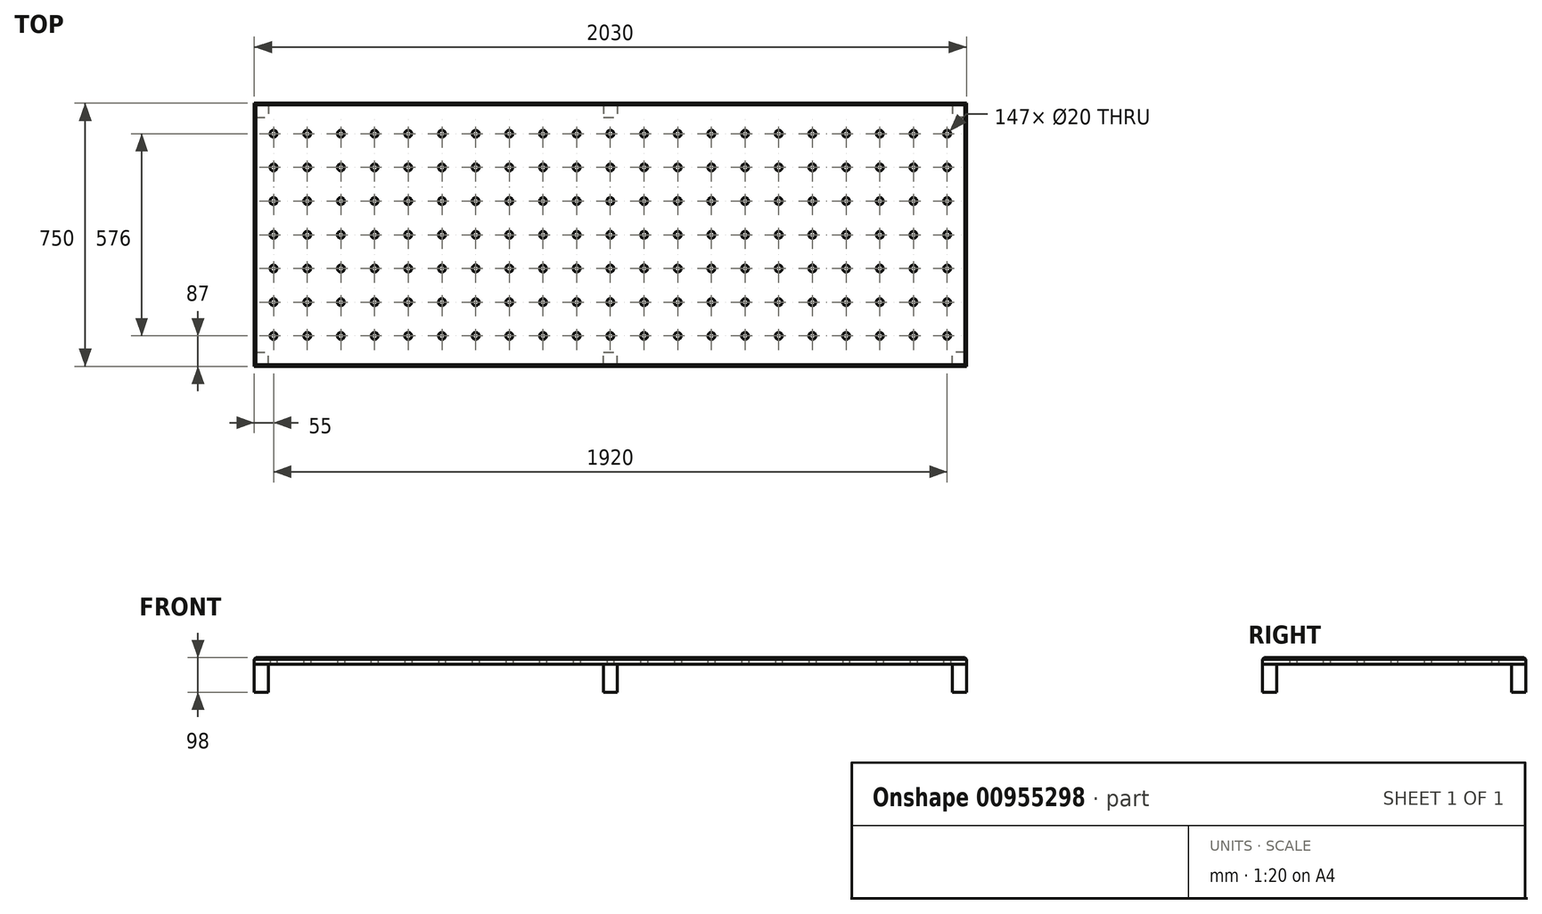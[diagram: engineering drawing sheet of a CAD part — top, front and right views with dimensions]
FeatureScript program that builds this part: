
annotation { "Feature Type Name" : "Feature", "Feature Type Description" : "" }
export const myFeature = defineFeature(function(context is Context, id is Id, definition is map)
    precondition{}
    {
        {
            var Q0;
            Q0=qCreatedBy(makeId("Top.planeOp"),FACE);
            var sketch = newSketch(context, id + "F0", { "sketchPlane" : qUnion([Q0])});
            skLineSegment(sketch, "E0.bottom", {"start": v(-1015, 375) * mm, "end": v(1015, 375) * mm});
            skLineSegment(sketch, "E0.top", {"start": v(-1015, -375) * mm, "end": v(1015, -375) * mm});
            skLineSegment(sketch, "E0.left", {"start": v(-1015, 375) * mm, "end": v(-1015, -375) * mm});
            skLineSegment(sketch, "E0.right", {"start": v(1015, 375) * mm, "end": v(1015, -375) * mm});
            skPoint(sketch, "E0.middle", {"position": v(0, 0) * mm});
            skLineSegment(sketch, "E1", {"start": v(-1321.87, 0) * mm, "end": v(1540.38, 0) * mm, "construction": true});
            skCircle(sketch, "E2", {"center": v(0, 0) * mm, "radius": 10 * mm});
            skCircle(sketch, "E3.0.1.0", {"center": v(0, 96) * mm, "radius": 10 * mm});
            skCircle(sketch, "E3.0.2.0", {"center": v(0, 192) * mm, "radius": 10 * mm});
            skCircle(sketch, "E3.0.3.0", {"center": v(0, 288) * mm, "radius": 10 * mm});
            skCircle(sketch, "E3.1.0.0", {"center": v(96, 0) * mm, "radius": 10 * mm});
            skCircle(sketch, "E3.1.1.0", {"center": v(96, 96) * mm, "radius": 10 * mm});
            skCircle(sketch, "E3.1.2.0", {"center": v(96, 192) * mm, "radius": 10 * mm});
            skCircle(sketch, "E3.1.3.0", {"center": v(96, 288) * mm, "radius": 10 * mm});
            skCircle(sketch, "E3.2.0.0", {"center": v(192, 0) * mm, "radius": 10 * mm});
            skCircle(sketch, "E3.2.1.0", {"center": v(192, 96) * mm, "radius": 10 * mm});
            skCircle(sketch, "E3.2.2.0", {"center": v(192, 192) * mm, "radius": 10 * mm});
            skCircle(sketch, "E3.2.3.0", {"center": v(192, 288) * mm, "radius": 10 * mm});
            skCircle(sketch, "E3.3.0.0", {"center": v(288, 0) * mm, "radius": 10 * mm});
            skCircle(sketch, "E3.3.1.0", {"center": v(288, 96) * mm, "radius": 10 * mm});
            skCircle(sketch, "E3.3.2.0", {"center": v(288, 192) * mm, "radius": 10 * mm});
            skCircle(sketch, "E3.3.3.0", {"center": v(288, 288) * mm, "radius": 10 * mm});
            skCircle(sketch, "E3.4.0.0", {"center": v(384, 0) * mm, "radius": 10 * mm});
            skCircle(sketch, "E3.4.1.0", {"center": v(384, 96) * mm, "radius": 10 * mm});
            skCircle(sketch, "E3.4.2.0", {"center": v(384, 192) * mm, "radius": 10 * mm});
            skCircle(sketch, "E3.4.3.0", {"center": v(384, 288) * mm, "radius": 10 * mm});
            skCircle(sketch, "E3.5.0.0", {"center": v(480, 0) * mm, "radius": 10 * mm});
            skCircle(sketch, "E3.5.1.0", {"center": v(480, 96) * mm, "radius": 10 * mm});
            skCircle(sketch, "E3.5.2.0", {"center": v(480, 192) * mm, "radius": 10 * mm});
            skCircle(sketch, "E3.5.3.0", {"center": v(480, 288) * mm, "radius": 10 * mm});
            skCircle(sketch, "E3.6.0.0", {"center": v(576, 0) * mm, "radius": 10 * mm});
            skCircle(sketch, "E3.6.1.0", {"center": v(576, 96) * mm, "radius": 10 * mm});
            skCircle(sketch, "E3.6.2.0", {"center": v(576, 192) * mm, "radius": 10 * mm});
            skCircle(sketch, "E3.6.3.0", {"center": v(576, 288) * mm, "radius": 10 * mm});
            skCircle(sketch, "E3.7.0.0", {"center": v(672, 0) * mm, "radius": 10 * mm});
            skCircle(sketch, "E3.7.1.0", {"center": v(672, 96) * mm, "radius": 10 * mm});
            skCircle(sketch, "E3.7.2.0", {"center": v(672, 192) * mm, "radius": 10 * mm});
            skCircle(sketch, "E3.7.3.0", {"center": v(672, 288) * mm, "radius": 10 * mm});
            skCircle(sketch, "E3.8.0.0", {"center": v(768, 0) * mm, "radius": 10 * mm});
            skCircle(sketch, "E3.8.1.0", {"center": v(768, 96) * mm, "radius": 10 * mm});
            skCircle(sketch, "E3.8.2.0", {"center": v(768, 192) * mm, "radius": 10 * mm});
            skCircle(sketch, "E3.8.3.0", {"center": v(768, 288) * mm, "radius": 10 * mm});
            skCircle(sketch, "E3.9.0.0", {"center": v(864, 0) * mm, "radius": 10 * mm});
            skCircle(sketch, "E3.9.1.0", {"center": v(864, 96) * mm, "radius": 10 * mm});
            skCircle(sketch, "E3.9.2.0", {"center": v(864, 192) * mm, "radius": 10 * mm});
            skCircle(sketch, "E3.9.3.0", {"center": v(864, 288) * mm, "radius": 10 * mm});
            skCircle(sketch, "E3.10.0.0", {"center": v(960, 0) * mm, "radius": 10 * mm});
            skCircle(sketch, "E3.10.1.0", {"center": v(960, 96) * mm, "radius": 10 * mm});
            skCircle(sketch, "E3.10.2.0", {"center": v(960, 192) * mm, "radius": 10 * mm});
            skCircle(sketch, "E3.10.3.0", {"center": v(960, 288) * mm, "radius": 10 * mm});
            skLineSegment(sketch, "E3.direction1", {"start": v(0, 0) * mm, "end": v(96, 0) * mm, "construction": true});
            skLineSegment(sketch, "E3.direction2", {"start": v(0, 0) * mm, "end": v(0, 96) * mm, "construction": true});
            skCircle(sketch, "E4.MirrorC", {"center": v(768, -96) * mm, "radius": 10 * mm});
            skCircle(sketch, "E5.MirrorC", {"center": v(480, -288) * mm, "radius": 10 * mm});
            skCircle(sketch, "E6.MirrorC", {"center": v(384, -192) * mm, "radius": 10 * mm});
            skCircle(sketch, "E7.MirrorC", {"center": v(96, -96) * mm, "radius": 10 * mm});
            skCircle(sketch, "E8.MirrorC", {"center": v(864, -192) * mm, "radius": 10 * mm});
            skCircle(sketch, "E9.MirrorC", {"center": v(96, -192) * mm, "radius": 10 * mm});
            skCircle(sketch, "E10.MirrorC", {"center": v(768, -192) * mm, "radius": 10 * mm});
            skCircle(sketch, "E11.MirrorC", {"center": v(192, -192) * mm, "radius": 10 * mm});
            skCircle(sketch, "E12.MirrorC", {"center": v(960, -192) * mm, "radius": 10 * mm});
            skCircle(sketch, "E13.MirrorC", {"center": v(960, -288) * mm, "radius": 10 * mm});
            skCircle(sketch, "E14.MirrorC", {"center": v(960, -96) * mm, "radius": 10 * mm});
            skCircle(sketch, "E15.MirrorC", {"center": v(192, -96) * mm, "radius": 10 * mm});
            skCircle(sketch, "E16.MirrorC", {"center": v(576, -288) * mm, "radius": 10 * mm});
            skCircle(sketch, "E17.MirrorC", {"center": v(192, -288) * mm, "radius": 10 * mm});
            skCircle(sketch, "E18.MirrorC", {"center": v(96, -288) * mm, "radius": 10 * mm});
            skCircle(sketch, "E19.MirrorC", {"center": v(672, -288) * mm, "radius": 10 * mm});
            skCircle(sketch, "E20.MirrorC", {"center": v(384, -288) * mm, "radius": 10 * mm});
            skCircle(sketch, "E21.MirrorC", {"center": v(576, -96) * mm, "radius": 10 * mm});
            skCircle(sketch, "E22.MirrorC", {"center": v(768, -288) * mm, "radius": 10 * mm});
            skCircle(sketch, "E23.MirrorC", {"center": v(480, -96) * mm, "radius": 10 * mm});
            skCircle(sketch, "E24.MirrorC", {"center": v(480, -192) * mm, "radius": 10 * mm});
            skCircle(sketch, "E25.MirrorC", {"center": v(288, -288) * mm, "radius": 10 * mm});
            skCircle(sketch, "E26.MirrorC", {"center": v(864, -288) * mm, "radius": 10 * mm});
            skCircle(sketch, "E27.MirrorC", {"center": v(384, -96) * mm, "radius": 10 * mm});
            skCircle(sketch, "E28.MirrorC", {"center": v(288, -96) * mm, "radius": 10 * mm});
            skCircle(sketch, "E29.MirrorC", {"center": v(288, -192) * mm, "radius": 10 * mm});
            skCircle(sketch, "E30.MirrorC", {"center": v(864, -96) * mm, "radius": 10 * mm});
            skCircle(sketch, "E31.MirrorC", {"center": v(576, -192) * mm, "radius": 10 * mm});
            skCircle(sketch, "E32.MirrorC", {"center": v(672, -192) * mm, "radius": 10 * mm});
            skCircle(sketch, "E33.MirrorC", {"center": v(672, -96) * mm, "radius": 10 * mm});
            skCircle(sketch, "E34.MirrorC", {"center": v(-96, 0) * mm, "radius": 10 * mm});
            skCircle(sketch, "E35.MirrorC", {"center": v(-960, 192) * mm, "radius": 10 * mm});
            skCircle(sketch, "E36.MirrorC", {"center": v(-480, 0) * mm, "radius": 10 * mm});
            skCircle(sketch, "E37.MirrorC", {"center": v(-192, 288) * mm, "radius": 10 * mm});
            skCircle(sketch, "E38.MirrorC", {"center": v(-480, 96) * mm, "radius": 10 * mm});
            skCircle(sketch, "E39.MirrorC", {"center": v(-768, 0) * mm, "radius": 10 * mm});
            skCircle(sketch, "E40.MirrorC", {"center": v(-768, -288) * mm, "radius": 10 * mm});
            skCircle(sketch, "E41.MirrorC", {"center": v(-480, 192) * mm, "radius": 10 * mm});
            skCircle(sketch, "E42.MirrorC", {"center": v(-576, 96) * mm, "radius": 10 * mm});
            skCircle(sketch, "E43.MirrorC", {"center": v(-672, 192) * mm, "radius": 10 * mm});
            skCircle(sketch, "E44.MirrorC", {"center": v(-960, -192) * mm, "radius": 10 * mm});
            skCircle(sketch, "E45.MirrorC", {"center": v(-960, 0) * mm, "radius": 10 * mm});
            skCircle(sketch, "E46.MirrorC", {"center": v(-480, -288) * mm, "radius": 10 * mm});
            skCircle(sketch, "E47.MirrorC", {"center": v(-768, -192) * mm, "radius": 10 * mm});
            skCircle(sketch, "E48.MirrorC", {"center": v(-960, 96) * mm, "radius": 10 * mm});
            skCircle(sketch, "E49.MirrorC", {"center": v(-768, 192) * mm, "radius": 10 * mm});
            skCircle(sketch, "E50.MirrorC", {"center": v(-288, 192) * mm, "radius": 10 * mm});
            skCircle(sketch, "E51.MirrorC", {"center": v(-288, -192) * mm, "radius": 10 * mm});
            skCircle(sketch, "E52.MirrorC", {"center": v(-192, -192) * mm, "radius": 10 * mm});
            skCircle(sketch, "E53.MirrorC", {"center": v(-288, 288) * mm, "radius": 10 * mm});
            skCircle(sketch, "E54.MirrorC", {"center": v(-192, 0) * mm, "radius": 10 * mm});
            skCircle(sketch, "E55.MirrorC", {"center": v(-672, 288) * mm, "radius": 10 * mm});
            skCircle(sketch, "E56.MirrorC", {"center": v(-576, 192) * mm, "radius": 10 * mm});
            skCircle(sketch, "E57.MirrorC", {"center": v(-672, -192) * mm, "radius": 10 * mm});
            skCircle(sketch, "E58.MirrorC", {"center": v(-768, -96) * mm, "radius": 10 * mm});
            skCircle(sketch, "E59.MirrorC", {"center": v(-384, -288) * mm, "radius": 10 * mm});
            skCircle(sketch, "E60.MirrorC", {"center": v(-384, -96) * mm, "radius": 10 * mm});
            skCircle(sketch, "E61.MirrorC", {"center": v(-192, -288) * mm, "radius": 10 * mm});
            skCircle(sketch, "E62.MirrorC", {"center": v(-864, 288) * mm, "radius": 10 * mm});
            skCircle(sketch, "E63.MirrorC", {"center": v(-576, -96) * mm, "radius": 10 * mm});
            skCircle(sketch, "E64.MirrorC", {"center": v(-480, -96) * mm, "radius": 10 * mm});
            skCircle(sketch, "E65.MirrorC", {"center": v(-864, 0) * mm, "radius": 10 * mm});
            skCircle(sketch, "E66.MirrorC", {"center": v(-96, -288) * mm, "radius": 10 * mm});
            skCircle(sketch, "E67.MirrorC", {"center": v(-672, -96) * mm, "radius": 10 * mm});
            skCircle(sketch, "E68.MirrorC", {"center": v(-192, 96) * mm, "radius": 10 * mm});
            skCircle(sketch, "E69.MirrorC", {"center": v(-288, -288) * mm, "radius": 10 * mm});
            skCircle(sketch, "E70.MirrorC", {"center": v(-288, 0) * mm, "radius": 10 * mm});
            skCircle(sketch, "E71.MirrorC", {"center": v(-96, 192) * mm, "radius": 10 * mm});
            skCircle(sketch, "E72.MirrorC", {"center": v(-864, 192) * mm, "radius": 10 * mm});
            skCircle(sketch, "E73.MirrorC", {"center": v(-96, 96) * mm, "radius": 10 * mm});
            skCircle(sketch, "E74.MirrorC", {"center": v(-192, -96) * mm, "radius": 10 * mm});
            skCircle(sketch, "E75.MirrorC", {"center": v(-96, 288) * mm, "radius": 10 * mm});
            skCircle(sketch, "E76.MirrorC", {"center": v(-960, 288) * mm, "radius": 10 * mm});
            skCircle(sketch, "E77.MirrorC", {"center": v(-864, -192) * mm, "radius": 10 * mm});
            skCircle(sketch, "E78.MirrorC", {"center": v(-672, -288) * mm, "radius": 10 * mm});
            skCircle(sketch, "E79.MirrorC", {"center": v(-960, -288) * mm, "radius": 10 * mm});
            skCircle(sketch, "E80.MirrorC", {"center": v(-384, 0) * mm, "radius": 10 * mm});
            skCircle(sketch, "E81.MirrorC", {"center": v(-480, 288) * mm, "radius": 10 * mm});
            skCircle(sketch, "E82.MirrorC", {"center": v(-864, 96) * mm, "radius": 10 * mm});
            skCircle(sketch, "E83.MirrorC", {"center": v(-960, -96) * mm, "radius": 10 * mm});
            skCircle(sketch, "E84.MirrorC", {"center": v(-96, -192) * mm, "radius": 10 * mm});
            skCircle(sketch, "E85.MirrorC", {"center": v(-480, -192) * mm, "radius": 10 * mm});
            skCircle(sketch, "E86.MirrorC", {"center": v(-576, 0) * mm, "radius": 10 * mm});
            skCircle(sketch, "E87.MirrorC", {"center": v(-384, -192) * mm, "radius": 10 * mm});
            skCircle(sketch, "E88.MirrorC", {"center": v(-384, 192) * mm, "radius": 10 * mm});
            skCircle(sketch, "E89.MirrorC", {"center": v(-768, 288) * mm, "radius": 10 * mm});
            skCircle(sketch, "E90.MirrorC", {"center": v(-384, 288) * mm, "radius": 10 * mm});
            skCircle(sketch, "E91.MirrorC", {"center": v(-288, -96) * mm, "radius": 10 * mm});
            skCircle(sketch, "E92.MirrorC", {"center": v(-576, -288) * mm, "radius": 10 * mm});
            skCircle(sketch, "E93.MirrorC", {"center": v(-96, -96) * mm, "radius": 10 * mm});
            skCircle(sketch, "E94.MirrorC", {"center": v(-672, 96) * mm, "radius": 10 * mm});
            skCircle(sketch, "E95.MirrorC", {"center": v(-576, 288) * mm, "radius": 10 * mm});
            skCircle(sketch, "E96.MirrorC", {"center": v(-672, 0) * mm, "radius": 10 * mm});
            skCircle(sketch, "E97.MirrorC", {"center": v(-192, 192) * mm, "radius": 10 * mm});
            skCircle(sketch, "E98.MirrorC", {"center": v(-288, 96) * mm, "radius": 10 * mm});
            skCircle(sketch, "E99.MirrorC", {"center": v(-864, -288) * mm, "radius": 10 * mm});
            skCircle(sketch, "E100.MirrorC", {"center": v(-768, 96) * mm, "radius": 10 * mm});
            skCircle(sketch, "E101.MirrorC", {"center": v(-864, -96) * mm, "radius": 10 * mm});
            skCircle(sketch, "E102.MirrorC", {"center": v(-576, -192) * mm, "radius": 10 * mm});
            skCircle(sketch, "E103.MirrorC", {"center": v(-384, 96) * mm, "radius": 10 * mm});
            skCircle(sketch, "E104.MirrorC", {"center": v(0, -288) * mm, "radius": 10 * mm});
            skCircle(sketch, "E105.MirrorC", {"center": v(0, -192) * mm, "radius": 10 * mm});
            skCircle(sketch, "E106.MirrorC", {"center": v(0, -96) * mm, "radius": 10 * mm});
            skSolve(sketch);
        }
        {
            var Q0;
            Q0 = qSketchRegion(id + "F0", true);
            extrude(context, id + "F1", {"entities" : qUnion([Q0]), "depth" : 18 * mm, "offsetDistance" : 25 * mm});
        }
        {
            var Q0;
            Q0=makeQuery(id+"F1.opExtrude","CAP_EDGE",EDGE,{"disambiguationData":[OSD([sQuery(id+"F0.wireOp",EDGE,"E0.bottom")])],"isStart":false});
            var Q1;
            Q1=makeQuery(id+"F1.opExtrude","CAP_EDGE",EDGE,{"disambiguationData":[OSD([sQuery(id+"F0.wireOp",EDGE,"E0.left")])],"isStart":false});
            var Q2;
            Q2=makeQuery(id+"F1.opExtrude","CAP_EDGE",EDGE,{"disambiguationData":[OSD([sQuery(id+"F0.wireOp",EDGE,"E0.top")])],"isStart":false});
            var Q3;
            Q3=makeQuery(id+"F1.opExtrude","CAP_EDGE",EDGE,{"disambiguationData":[OSD([sQuery(id+"F0.wireOp",EDGE,"E0.right")])],"isStart":false});
            chamfer(context, id + "F2", {"entities" : qUnion([Q0, Q1, Q2, Q3]), "width" : 5 * mm, "tangentPropagation" : true});
        }
        {
            var Q0;
            Q0=makeQuery(id+"F1.opExtrude","CAP_FACE",FACE,{"disambiguationData":[OSD([sQuery(id+"F0.wireOp",EDGE,"E0.bottom"),sQuery(id+"F0.wireOp",EDGE,"E0.top"),sQuery(id+"F0.wireOp",EDGE,"E0.left"),sQuery(id+"F0.wireOp",EDGE,"E0.right"),sQuery(id+"F0.wireOp",EDGE,"E2"),sQuery(id+"F0.wireOp",EDGE,"E3.0.1.0"),sQuery(id+"F0.wireOp",EDGE,"E3.0.2.0"),sQuery(id+"F0.wireOp",EDGE,"E3.0.3.0"),sQuery(id+"F0.wireOp",EDGE,"E3.1.0.0"),sQuery(id+"F0.wireOp",EDGE,"E3.1.1.0"),sQuery(id+"F0.wireOp",EDGE,"E3.1.2.0"),sQuery(id+"F0.wireOp",EDGE,"E3.1.3.0"),sQuery(id+"F0.wireOp",EDGE,"E3.2.0.0"),sQuery(id+"F0.wireOp",EDGE,"E3.2.1.0"),sQuery(id+"F0.wireOp",EDGE,"E3.2.2.0"),sQuery(id+"F0.wireOp",EDGE,"E3.2.3.0"),sQuery(id+"F0.wireOp",EDGE,"E3.3.0.0"),sQuery(id+"F0.wireOp",EDGE,"E3.3.1.0"),sQuery(id+"F0.wireOp",EDGE,"E3.3.2.0"),sQuery(id+"F0.wireOp",EDGE,"E3.3.3.0"),sQuery(id+"F0.wireOp",EDGE,"E3.4.0.0"),sQuery(id+"F0.wireOp",EDGE,"E3.4.1.0"),sQuery(id+"F0.wireOp",EDGE,"E3.4.2.0"),sQuery(id+"F0.wireOp",EDGE,"E3.4.3.0"),sQuery(id+"F0.wireOp",EDGE,"E3.5.0.0"),sQuery(id+"F0.wireOp",EDGE,"E3.5.1.0"),sQuery(id+"F0.wireOp",EDGE,"E3.5.2.0"),sQuery(id+"F0.wireOp",EDGE,"E3.5.3.0"),sQuery(id+"F0.wireOp",EDGE,"E3.6.0.0"),sQuery(id+"F0.wireOp",EDGE,"E3.6.1.0"),sQuery(id+"F0.wireOp",EDGE,"E3.6.2.0"),sQuery(id+"F0.wireOp",EDGE,"E3.6.3.0"),sQuery(id+"F0.wireOp",EDGE,"E3.7.0.0"),sQuery(id+"F0.wireOp",EDGE,"E3.7.1.0"),sQuery(id+"F0.wireOp",EDGE,"E3.7.2.0"),sQuery(id+"F0.wireOp",EDGE,"E3.7.3.0"),sQuery(id+"F0.wireOp",EDGE,"E3.8.0.0"),sQuery(id+"F0.wireOp",EDGE,"E3.8.1.0"),sQuery(id+"F0.wireOp",EDGE,"E3.8.2.0"),sQuery(id+"F0.wireOp",EDGE,"E3.8.3.0"),sQuery(id+"F0.wireOp",EDGE,"E3.9.0.0"),sQuery(id+"F0.wireOp",EDGE,"E3.9.1.0"),sQuery(id+"F0.wireOp",EDGE,"E3.9.2.0"),sQuery(id+"F0.wireOp",EDGE,"E3.9.3.0"),sQuery(id+"F0.wireOp",EDGE,"E3.10.0.0"),sQuery(id+"F0.wireOp",EDGE,"E3.10.1.0"),sQuery(id+"F0.wireOp",EDGE,"E3.10.2.0"),sQuery(id+"F0.wireOp",EDGE,"E3.10.3.0"),sQuery(id+"F0.wireOp",EDGE,"E4.MirrorC"),sQuery(id+"F0.wireOp",EDGE,"E5.MirrorC"),sQuery(id+"F0.wireOp",EDGE,"E6.MirrorC"),sQuery(id+"F0.wireOp",EDGE,"E7.MirrorC"),sQuery(id+"F0.wireOp",EDGE,"E8.MirrorC"),sQuery(id+"F0.wireOp",EDGE,"E9.MirrorC"),sQuery(id+"F0.wireOp",EDGE,"E10.MirrorC"),sQuery(id+"F0.wireOp",EDGE,"E11.MirrorC"),sQuery(id+"F0.wireOp",EDGE,"E12.MirrorC"),sQuery(id+"F0.wireOp",EDGE,"E13.MirrorC"),sQuery(id+"F0.wireOp",EDGE,"E14.MirrorC"),sQuery(id+"F0.wireOp",EDGE,"E15.MirrorC"),sQuery(id+"F0.wireOp",EDGE,"E16.MirrorC"),sQuery(id+"F0.wireOp",EDGE,"E17.MirrorC"),sQuery(id+"F0.wireOp",EDGE,"E18.MirrorC"),sQuery(id+"F0.wireOp",EDGE,"E19.MirrorC"),sQuery(id+"F0.wireOp",EDGE,"E20.MirrorC"),sQuery(id+"F0.wireOp",EDGE,"E21.MirrorC"),sQuery(id+"F0.wireOp",EDGE,"E22.MirrorC"),sQuery(id+"F0.wireOp",EDGE,"E23.MirrorC"),sQuery(id+"F0.wireOp",EDGE,"E24.MirrorC"),sQuery(id+"F0.wireOp",EDGE,"E25.MirrorC"),sQuery(id+"F0.wireOp",EDGE,"E26.MirrorC"),sQuery(id+"F0.wireOp",EDGE,"E27.MirrorC"),sQuery(id+"F0.wireOp",EDGE,"E28.MirrorC"),sQuery(id+"F0.wireOp",EDGE,"E29.MirrorC"),sQuery(id+"F0.wireOp",EDGE,"E30.MirrorC"),sQuery(id+"F0.wireOp",EDGE,"E31.MirrorC"),sQuery(id+"F0.wireOp",EDGE,"E32.MirrorC"),sQuery(id+"F0.wireOp",EDGE,"E33.MirrorC"),sQuery(id+"F0.wireOp",EDGE,"E34.MirrorC"),sQuery(id+"F0.wireOp",EDGE,"E35.MirrorC"),sQuery(id+"F0.wireOp",EDGE,"E36.MirrorC"),sQuery(id+"F0.wireOp",EDGE,"E37.MirrorC"),sQuery(id+"F0.wireOp",EDGE,"E38.MirrorC"),sQuery(id+"F0.wireOp",EDGE,"E39.MirrorC"),sQuery(id+"F0.wireOp",EDGE,"E40.MirrorC"),sQuery(id+"F0.wireOp",EDGE,"E41.MirrorC"),sQuery(id+"F0.wireOp",EDGE,"E42.MirrorC"),sQuery(id+"F0.wireOp",EDGE,"E43.MirrorC"),sQuery(id+"F0.wireOp",EDGE,"E44.MirrorC"),sQuery(id+"F0.wireOp",EDGE,"E45.MirrorC"),sQuery(id+"F0.wireOp",EDGE,"E46.MirrorC"),sQuery(id+"F0.wireOp",EDGE,"E47.MirrorC"),sQuery(id+"F0.wireOp",EDGE,"E48.MirrorC"),sQuery(id+"F0.wireOp",EDGE,"E49.MirrorC"),sQuery(id+"F0.wireOp",EDGE,"E50.MirrorC"),sQuery(id+"F0.wireOp",EDGE,"E51.MirrorC"),sQuery(id+"F0.wireOp",EDGE,"E52.MirrorC"),sQuery(id+"F0.wireOp",EDGE,"E53.MirrorC"),sQuery(id+"F0.wireOp",EDGE,"E54.MirrorC"),sQuery(id+"F0.wireOp",EDGE,"E55.MirrorC"),sQuery(id+"F0.wireOp",EDGE,"E56.MirrorC"),sQuery(id+"F0.wireOp",EDGE,"E57.MirrorC"),sQuery(id+"F0.wireOp",EDGE,"E58.MirrorC"),sQuery(id+"F0.wireOp",EDGE,"E59.MirrorC"),sQuery(id+"F0.wireOp",EDGE,"E60.MirrorC"),sQuery(id+"F0.wireOp",EDGE,"E61.MirrorC"),sQuery(id+"F0.wireOp",EDGE,"E62.MirrorC"),sQuery(id+"F0.wireOp",EDGE,"E63.MirrorC"),sQuery(id+"F0.wireOp",EDGE,"E64.MirrorC"),sQuery(id+"F0.wireOp",EDGE,"E65.MirrorC"),sQuery(id+"F0.wireOp",EDGE,"E66.MirrorC"),sQuery(id+"F0.wireOp",EDGE,"E67.MirrorC"),sQuery(id+"F0.wireOp",EDGE,"E68.MirrorC"),sQuery(id+"F0.wireOp",EDGE,"E69.MirrorC"),sQuery(id+"F0.wireOp",EDGE,"E70.MirrorC"),sQuery(id+"F0.wireOp",EDGE,"E71.MirrorC"),sQuery(id+"F0.wireOp",EDGE,"E72.MirrorC"),sQuery(id+"F0.wireOp",EDGE,"E73.MirrorC"),sQuery(id+"F0.wireOp",EDGE,"E74.MirrorC"),sQuery(id+"F0.wireOp",EDGE,"E75.MirrorC"),sQuery(id+"F0.wireOp",EDGE,"E76.MirrorC"),sQuery(id+"F0.wireOp",EDGE,"E77.MirrorC"),sQuery(id+"F0.wireOp",EDGE,"E78.MirrorC"),sQuery(id+"F0.wireOp",EDGE,"E79.MirrorC"),sQuery(id+"F0.wireOp",EDGE,"E80.MirrorC"),sQuery(id+"F0.wireOp",EDGE,"E81.MirrorC"),sQuery(id+"F0.wireOp",EDGE,"E82.MirrorC"),sQuery(id+"F0.wireOp",EDGE,"E83.MirrorC"),sQuery(id+"F0.wireOp",EDGE,"E84.MirrorC"),sQuery(id+"F0.wireOp",EDGE,"E85.MirrorC"),sQuery(id+"F0.wireOp",EDGE,"E86.MirrorC"),sQuery(id+"F0.wireOp",EDGE,"E87.MirrorC"),sQuery(id+"F0.wireOp",EDGE,"E88.MirrorC"),sQuery(id+"F0.wireOp",EDGE,"E89.MirrorC"),sQuery(id+"F0.wireOp",EDGE,"E90.MirrorC"),sQuery(id+"F0.wireOp",EDGE,"E91.MirrorC"),sQuery(id+"F0.wireOp",EDGE,"E92.MirrorC"),sQuery(id+"F0.wireOp",EDGE,"E93.MirrorC"),sQuery(id+"F0.wireOp",EDGE,"E94.MirrorC"),sQuery(id+"F0.wireOp",EDGE,"E95.MirrorC"),sQuery(id+"F0.wireOp",EDGE,"E96.MirrorC"),sQuery(id+"F0.wireOp",EDGE,"E97.MirrorC"),sQuery(id+"F0.wireOp",EDGE,"E98.MirrorC"),sQuery(id+"F0.wireOp",EDGE,"E99.MirrorC"),sQuery(id+"F0.wireOp",EDGE,"E100.MirrorC"),sQuery(id+"F0.wireOp",EDGE,"E101.MirrorC"),sQuery(id+"F0.wireOp",EDGE,"E102.MirrorC"),sQuery(id+"F0.wireOp",EDGE,"E103.MirrorC"),sQuery(id+"F0.wireOp",EDGE,"E104.MirrorC"),sQuery(id+"F0.wireOp",EDGE,"E105.MirrorC"),sQuery(id+"F0.wireOp",EDGE,"E106.MirrorC")])],"isStart":true});
            var sketch = newSketch(context, id + "F3", { "sketchPlane" : qUnion([Q0])});
            skLineSegment(sketch, "E107.bottom", {"start": v(-1015, 375) * mm, "end": v(-975, 375) * mm});
            skLineSegment(sketch, "E107.top", {"start": v(-1015, 335) * mm, "end": v(-975, 335) * mm});
            skLineSegment(sketch, "E107.left", {"start": v(-1015, 375) * mm, "end": v(-1015, 335) * mm});
            skLineSegment(sketch, "E107.right", {"start": v(-975, 375) * mm, "end": v(-975, 335) * mm});
            skLineSegment(sketch, "E108.MirrorCS", {"start": v(1015, 335) * mm, "end": v(975, 335) * mm});
            skLineSegment(sketch, "E109.MirrorCS", {"start": v(1015, 375) * mm, "end": v(1015, 335) * mm});
            skLineSegment(sketch, "E110.MirrorCS", {"start": v(975, 375) * mm, "end": v(975, 335) * mm});
            skLineSegment(sketch, "E111.MirrorCS", {"start": v(1015, 375) * mm, "end": v(975, 375) * mm});
            skLineSegment(sketch, "E112.MirrorCS", {"start": v(-1015, -335) * mm, "end": v(-975, -335) * mm});
            skLineSegment(sketch, "E113.MirrorCS", {"start": v(-975, -375) * mm, "end": v(-975, -335) * mm});
            skLineSegment(sketch, "E114.MirrorCS", {"start": v(-1015, -375) * mm, "end": v(-1015, -335) * mm});
            skLineSegment(sketch, "E115.MirrorCS", {"start": v(-1015, -375) * mm, "end": v(-975, -375) * mm});
            skLineSegment(sketch, "E116.MirrorCS", {"start": v(1015, -375) * mm, "end": v(1015, -335) * mm});
            skLineSegment(sketch, "E117.MirrorCS", {"start": v(1015, -335) * mm, "end": v(975, -335) * mm});
            skLineSegment(sketch, "E118.MirrorCS", {"start": v(1015, -375) * mm, "end": v(975, -375) * mm});
            skLineSegment(sketch, "E119.MirrorCS", {"start": v(975, -375) * mm, "end": v(975, -335) * mm});
            skLineSegment(sketch, "E120", {"start": v(0, 0) * mm, "end": v(0, 697.62) * mm, "construction": true});
            skLineSegment(sketch, "E121.bottom", {"start": v(-20, 375) * mm, "end": v(20, 375) * mm});
            skLineSegment(sketch, "E121.top", {"start": v(-20, 335) * mm, "end": v(20, 335) * mm});
            skLineSegment(sketch, "E121.left", {"start": v(-20, 375) * mm, "end": v(-20, 335) * mm});
            skLineSegment(sketch, "E121.right", {"start": v(20, 375) * mm, "end": v(20, 335) * mm});
            skPoint(sketch, "E121.middle", {"position": v(0, 355) * mm});
            skPoint(sketch, "E122.MirrorP", {"position": v(0, -355) * mm});
            skLineSegment(sketch, "E123.MirrorCS", {"start": v(20, -375) * mm, "end": v(20, -335) * mm});
            skLineSegment(sketch, "E124.MirrorCS", {"start": v(-20, -335) * mm, "end": v(20, -335) * mm});
            skLineSegment(sketch, "E125.MirrorCS", {"start": v(-20, -375) * mm, "end": v(20, -375) * mm});
            skLineSegment(sketch, "E126.MirrorCS", {"start": v(-20, -375) * mm, "end": v(-20, -335) * mm});
            skSolve(sketch);
        }
        {
            var Q0;
            Q0 = qSketchRegion(id + "F3", true);
            extrude(context, id + "F4", {"entities" : qUnion([Q0]), "depth" : 80 * mm, "offsetDistance" : 25 * mm});
        }
        {
            var Q0;
            Q0 = qSketchRegion(id + "F3", true);
            extrude(context, id + "F5", {"entities" : qUnion([Q0]), "depth" : 80 * mm, "offsetDistance" : 25 * mm});
        }
    });
